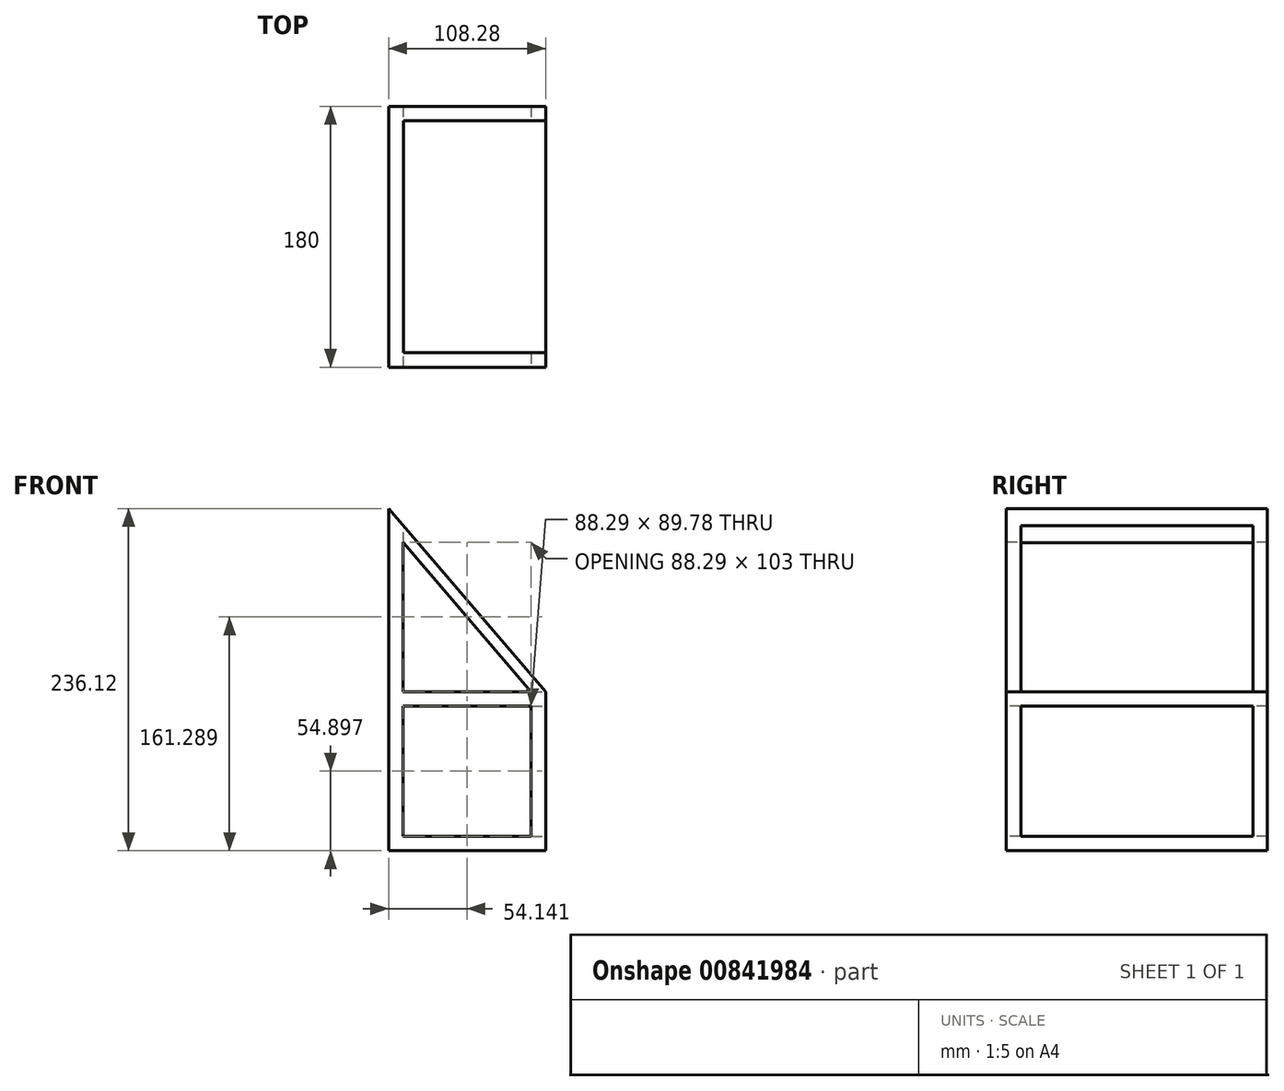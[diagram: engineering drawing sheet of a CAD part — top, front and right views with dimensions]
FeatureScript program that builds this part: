
annotation { "Feature Type Name" : "Feature", "Feature Type Description" : "" }
export const myFeature = defineFeature(function(context is Context, id is Id, definition is map)
    precondition{}
    {
        {
            var Q0;
            Q0=qCreatedBy(makeId("Front.planeOp"),FACE);
            var sketch = newSketch(context, id + "F0", { "sketchPlane" : qUnion([Q0])});
            skLineSegment(sketch, "E0", {"start": v(-79.04, 5.19) * mm, "end": v(-79.04, -85.65) * mm});
            skLineSegment(sketch, "E1", {"start": v(-79.04, 5.19) * mm, "end": v(-79.04, 168.99) * mm});
            skPoint(sketch, "E2.startSnap0", {"position": v(165.69, -59.65) * mm});
            skLineSegment(sketch, "E3", {"start": v(39.24, -59.65) * mm, "end": v(39.24, 30.99) * mm});
            skLineSegment(sketch, "E4", {"start": v(39.24, -59.65) * mm, "end": v(39.24, -85.65) * mm});
            skLineSegment(sketch, "E5", {"start": v(-79.04, -85.65) * mm, "end": v(39.24, -85.65) * mm});
            skLineSegment(sketch, "E6", {"start": v(-79.04, 168.99) * mm, "end": v(39.24, 30.99) * mm});
            skLineSegment(sketch, "E7.0", {"start": v(-74.04, 5.19) * mm, "end": v(-74.04, 155.47) * mm});
            skLineSegment(sketch, "E7.1", {"start": v(34.24, -59.65) * mm, "end": v(34.24, 29.14) * mm});
            skLineSegment(sketch, "E7.2", {"start": v(34.24, -59.65) * mm, "end": v(34.24, -80.65) * mm});
            skLineSegment(sketch, "E7.3", {"start": v(-74.04, 155.47) * mm, "end": v(34.24, 29.14) * mm});
            skLineSegment(sketch, "E7.4", {"start": v(-74.04, -80.65) * mm, "end": v(34.24, -80.65) * mm});
            skLineSegment(sketch, "E7.5", {"start": v(-74.04, 5.19) * mm, "end": v(-74.04, -80.65) * mm});
            skSolve(sketch);
        }
        {
            var Q0;
            Q0=makeQuery(id+"F0.imprint","IMPRINT",FACE,{"disambiguationData":[TD([[makeQuery(id+"F0.imprint","IMPRINT",EDGE,{"derivedFrom":sQuery(id+"F0.wireOp",EDGE,"E7.0")}),-1.0]])]});
            extrude(context, id + "F1", {"entities" : qUnion([Q0]), "depth" : 180 * mm, "offsetDistance" : 25 * mm});
        }
        {
            var Q0;
            Q0=makeQuery(id+"F1.opExtrude","CAP_FACE",FACE,{"disambiguationData":[OSD([sQuery(id+"F0.wireOp",EDGE,"E7.0"),sQuery(id+"F0.wireOp",EDGE,"E7.1"),sQuery(id+"F0.wireOp",EDGE,"E7.2"),sQuery(id+"F0.wireOp",EDGE,"E7.3"),sQuery(id+"F0.wireOp",EDGE,"E7.4"),sQuery(id+"F0.wireOp",EDGE,"E7.5")])],"isStart":false});
            var sketch = newSketch(context, id + "F2", { "sketchPlane" : qUnion([Q0])});
            skLineSegment(sketch, "E8", {"start": v(-74.04, -80.65) * mm, "end": v(-64.04, -80.65) * mm});
            skLineSegment(sketch, "E9", {"start": v(-64.04, -80.65) * mm, "end": v(-64.04, 143.8) * mm});
            skLineSegment(sketch, "E10", {"start": v(-74.04, -80.65) * mm, "end": v(-74.04, -70.65) * mm});
            skLineSegment(sketch, "E11", {"start": v(-74.04, -70.65) * mm, "end": v(34.24, -70.65) * mm});
            skLineSegment(sketch, "E12.bottom", {"start": v(34.24, 29.14) * mm, "end": v(-64.04, 29.14) * mm});
            skLineSegment(sketch, "E12.top", {"start": v(34.24, 19.14) * mm, "end": v(-64.04, 19.14) * mm});
            skLineSegment(sketch, "E12.left", {"start": v(34.24, 29.14) * mm, "end": v(34.24, 19.14) * mm});
            skLineSegment(sketch, "E12.right", {"start": v(-64.04, 29.14) * mm, "end": v(-64.04, 19.14) * mm});
            skLineSegment(sketch, "E13", {"start": v(34.24, 29.14) * mm, "end": v(24.24, 29.14) * mm});
            skLineSegment(sketch, "E14", {"start": v(24.24, 29.14) * mm, "end": v(-64.04, 132.14) * mm});
            skLineSegment(sketch, "E15", {"start": v(24.24, 29.14) * mm, "end": v(24.24, -70.65) * mm});
            skSolve(sketch);
        }
        {
            var Q0;
            {var subQ0=sQuery(id+"F2.wireOp",EDGE,"E12.bottom");Q0=makeQuery(id+"F2.imprint","IMPRINT",FACE,{"disambiguationData":[TD([[makeQuery(id+"F2.imprint","IMPRINT",EDGE,{"derivedFrom":subQ0}),-1.0]])]});}
            var Q1;
            {var subQ3=sQuery(id+"F2.wireOp",EDGE,"E11");var subQ5=sQuery(id+"F2.wireOp",EDGE,"E15");var subQ6=makeQuery(id+"F2.imprint","INTERSECT",VERTEX,{"derivedFrom":[subQ3,subQ5]});Q1=makeQuery(id+"F2.imprint","IMPRINT",FACE,{"disambiguationData":[TD([[makeQuery(id+"F2.imprint","IMPRINT",EDGE,{"disambiguationData":[TD([[subQ6,1.0]])],"derivedFrom":subQ3}),1.0]])]});}
            extrude(context, id + "F3", {"entities" : qUnion([Q0, Q1]), "operationType" : NewBodyOperationType.REMOVE, "oppositeDirection" : true, "depth" : 294 * mm, "offsetDistance" : 25 * mm});
        }
        {
            var Q0;
            Q0=makeQuery(id+"F1.opExtrude","SWEPT_FACE",FACE,{"disambiguationData":[OSD([sQuery(id+"F0.wireOp",EDGE,"E7.1"),sQuery(id+"F0.wireOp",EDGE,"E7.2")])]});
            var sketch = newSketch(context, id + "F4", { "sketchPlane" : qUnion([Q0])});
            skLineSegment(sketch, "E16", {"start": v(-180, -80.65) * mm, "end": v(-170, -80.65) * mm});
            skLineSegment(sketch, "E17", {"start": v(0, -80.65) * mm, "end": v(-10, -80.65) * mm});
            skLineSegment(sketch, "E18.bottom", {"start": v(-170, -80.65) * mm, "end": v(-10, -80.65) * mm});
            skLineSegment(sketch, "E18.top", {"start": v(-170, 199.1) * mm, "end": v(-10, 199.1) * mm});
            skLineSegment(sketch, "E18.left", {"start": v(-170, -80.65) * mm, "end": v(-170, 199.1) * mm});
            skLineSegment(sketch, "E18.right", {"start": v(-10, -80.65) * mm, "end": v(-10, 199.1) * mm});
            skLineSegment(sketch, "E19", {"start": v(-170, 29.14) * mm, "end": v(-170, 19.14) * mm});
            skLineSegment(sketch, "E20", {"start": v(-170, 19.14) * mm, "end": v(-10, 19.14) * mm});
            skLineSegment(sketch, "E21", {"start": v(-10, 19.14) * mm, "end": v(-10, 29.14) * mm});
            skLineSegment(sketch, "E22", {"start": v(-10, 29.14) * mm, "end": v(-170, 29.14) * mm});
            skLineSegment(sketch, "E23", {"start": v(-180, -80.65) * mm, "end": v(-180, -70.65) * mm});
            skLineSegment(sketch, "E24", {"start": v(-180, -70.65) * mm, "end": v(0, -70.65) * mm});
            skSolve(sketch);
        }
        {
            var Q0;
            {var subQ0=sQuery(id+"F4.wireOp",EDGE,"E20");Q0=makeQuery(id+"F4.imprint","IMPRINT",FACE,{"disambiguationData":[TD([[makeQuery(id+"F4.imprint","IMPRINT",EDGE,{"derivedFrom":subQ0}),-1.0]])]});}
            var Q1;
            {var subQ0=sQuery(id+"F4.wireOp",EDGE,"E18.top");Q1=makeQuery(id+"F4.imprint","IMPRINT",FACE,{"disambiguationData":[TD([[makeQuery(id+"F4.imprint","IMPRINT",EDGE,{"derivedFrom":subQ0}),-1.0]])]});}
            extrude(context, id + "F5", {"entities" : qUnion([Q0, Q1]), "operationType" : NewBodyOperationType.REMOVE, "oppositeDirection" : true, "depth" : 98 * mm, "offsetDistance" : 25 * mm});
        }
    });
